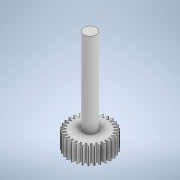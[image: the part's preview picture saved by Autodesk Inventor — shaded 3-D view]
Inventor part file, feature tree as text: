
AUTODESK INVENTOR PART (.ipt)
format: ipt  version: 2022 (Build 260153000, 153)  size: 282,624 bytes
history: native  units: mm
features: extrude x3, sketch x3, other x1, pattern_circular x1
ambient origin geometry x8: Origin, YZ Plane, XZ Plane, XY Plane, X Axis, Y Axis, Z Axis, Center Point
bodies: Body1 (feature_tree)
feature tree (8):
  other  "Bryła1"
  extrude  "Wyciągnięcie proste1"  Depth=15.0mm
  extrude  "Wyciągnięcie proste2"  Depth=101.0mm TaperAngle=0.0deg
  extrude  "Wyciągnięcie proste3"  Depth=40.0mm
  pattern_circular  "Szyk kołowy1"  Count=2  [1 undecoded]
  sketch  "Szkic1"
  sketch  "Szkic2"
  sketch  "Szkic3"
note: 1 required parameter value undecoded (feature->parameter linkage not recoverable at this tier; creation-order binding heuristic only, values carry confidence <= 0.55)
